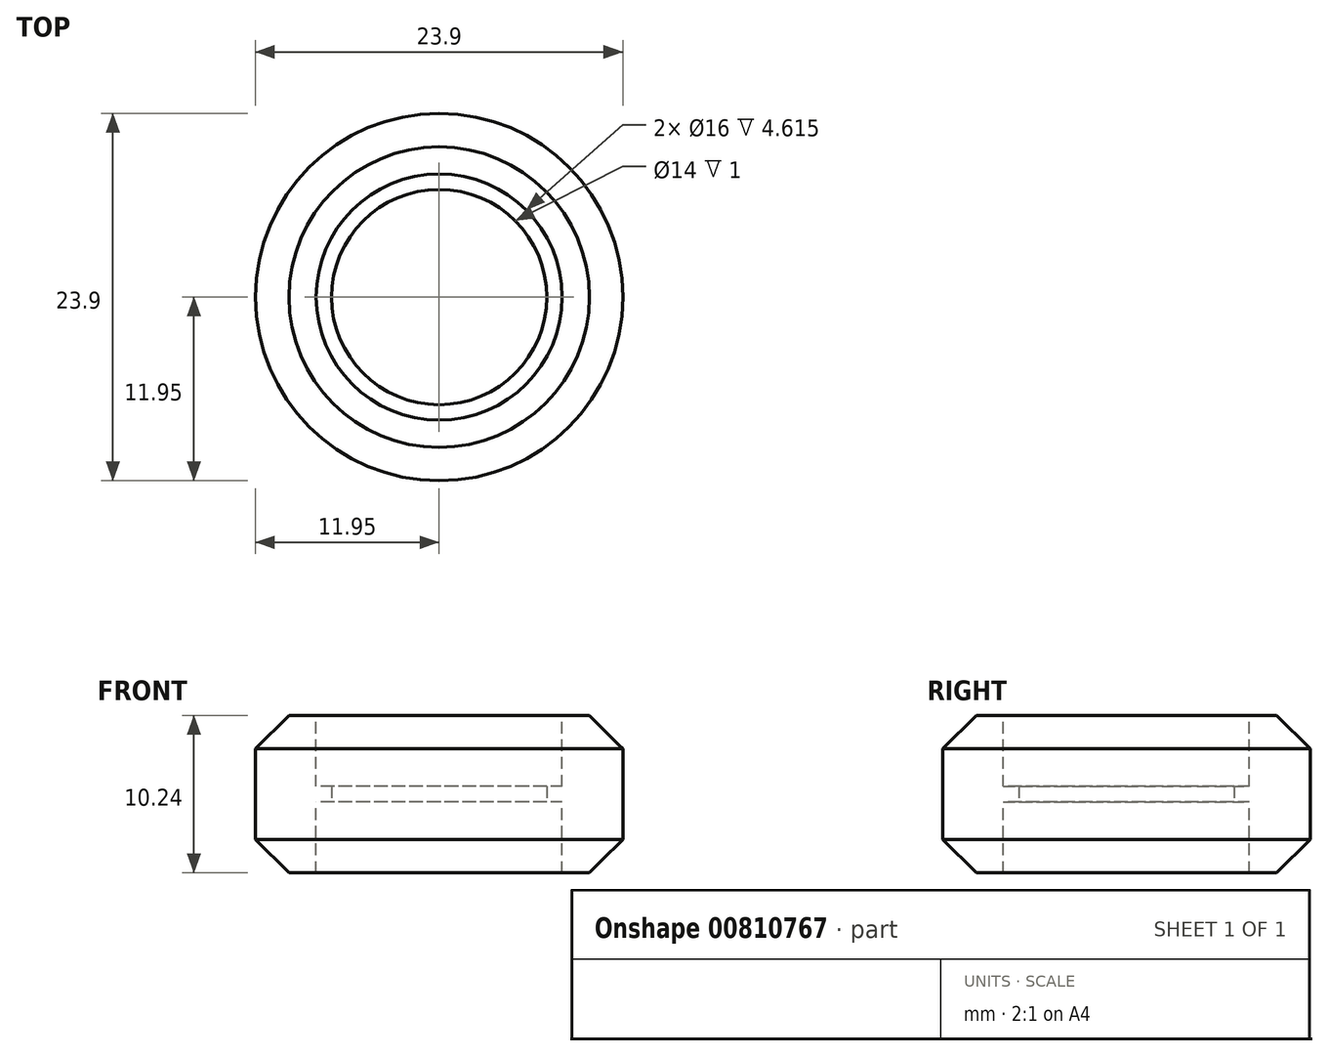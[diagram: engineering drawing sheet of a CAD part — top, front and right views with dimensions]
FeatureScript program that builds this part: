
annotation { "Feature Type Name" : "Feature", "Feature Type Description" : "" }
export const myFeature = defineFeature(function(context is Context, id is Id, definition is map)
    precondition{}
    {
        {
            var Q0;
            Q0=qCreatedBy(makeId("Front.planeOp"),FACE);
            var sketch = newSketch(context, id + "F0", { "sketchPlane" : qUnion([Q0])});
            skLineSegment(sketch, "E0.bottom", {"start": v(0, 5.11) * mm, "end": v(9.77, 5.11) * mm});
            skLineSegment(sketch, "E0.top", {"start": v(0, -5.11) * mm, "end": v(9.77, -5.11) * mm});
            skLineSegment(sketch, "E0.left", {"start": v(0, 5.11) * mm, "end": v(0, -5.11) * mm});
            skLineSegment(sketch, "E0.right", {"start": v(9.77, 5.11) * mm, "end": v(9.77, -5.11) * mm, "construction": true});
            skLineSegment(sketch, "E1", {"start": v(9.77, 5.11) * mm, "end": v(11.94, 2.94) * mm});
            skLineSegment(sketch, "E2", {"start": v(11.95, 2.94) * mm, "end": v(11.95, -2.94) * mm});
            skLineSegment(sketch, "E3", {"start": v(11.94, -2.94) * mm, "end": v(9.77, -5.11) * mm});
            skSolve(sketch);
        }
        {
            var Q0;
            Q0=makeQuery(id+"F0.imprint","IMPRINT",FACE,{"disambiguationData":[TD([[makeQuery(id+"F0.imprint","IMPRINT",EDGE,{"derivedFrom":sQuery(id+"F0.wireOp",EDGE,"E0.bottom")}),-1.0]])]});
            var Q1;
            Q1=sQuery(id+"F0.wireOp",EDGE,"E0.left");
            revolve(context, id + "F1", {"entities" : qUnion([Q0]), "axis" : qUnion([Q1]), "revolveType" : RevolveType.FULL});
        }
        {
            var Q0;
            Q0=qCreatedBy(makeId("Top.planeOp"),FACE);
            var sketch = newSketch(context, id + "F2", { "sketchPlane" : qUnion([Q0])});
            skCircle(sketch, "E4", {"center": v(0, 0) * mm, "radius": 8 * mm});
            skSolve(sketch);
        }
        {
            var Q0;
            Q0=qSketchRegion(id+"F2",true);
            extrude(context, id + "F3", {"entities" : qUnion([Q0]), "operationType" : NewBodyOperationType.REMOVE, "endBound" : BoundingType.THROUGH_ALL, "oppositeDirection" : true, "depth" : 25 * mm, "hasSecondDirection" : true, "secondDirectionBound" : BoundingType.THROUGH_ALL, "secondDirectionOppositeDirection" : false, "secondDirectionDepth" : 25 * mm});
        }
        {
            var Q0;
            Q0=qCreatedBy(makeId("Top.planeOp"),FACE);
            var sketch = newSketch(context, id + "F4", { "sketchPlane" : qUnion([Q0])});
            skCircle(sketch, "E5", {"center": v(0, 0) * mm, "radius": 7 * mm});
            skCircle(sketch, "E6.0", {"center": v(0, 0) * mm, "radius": 8 * mm});
            skSolve(sketch);
        }
        {
            var Q0;
            Q0=qSketchRegion(id+"F4",true);
            extrude(context, id + "F5", {"entities" : qUnion([Q0]), "operationType" : NewBodyOperationType.ADD, "depth" : 1 * mm, "symmetric" : true});
        }
    });
